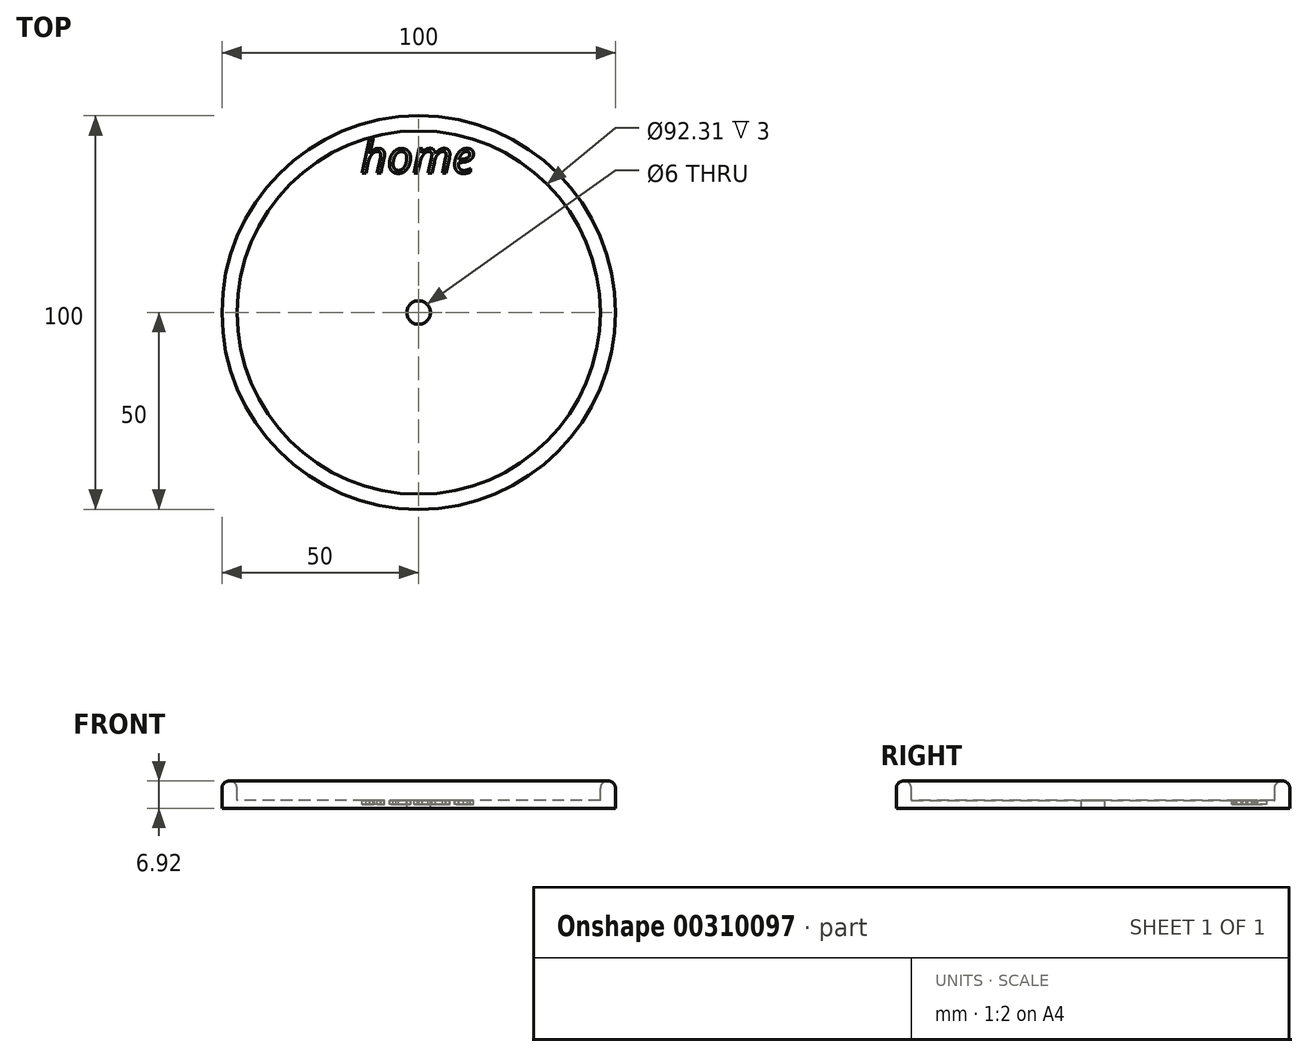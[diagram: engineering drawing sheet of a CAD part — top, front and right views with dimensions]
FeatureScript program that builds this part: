
annotation { "Feature Type Name" : "Feature", "Feature Type Description" : "" }
export const myFeature = defineFeature(function(context is Context, id is Id, definition is map)
    precondition{}
    {
        {
            var Q0;
            Q0=qCreatedBy(makeId("Front.planeOp"),FACE);
            var sketch = newSketch(context, id + "F0", { "sketchPlane" : qUnion([Q0])});
            skLineSegment(sketch, "E0", {"start": v(0, 11.93) * mm, "end": v(0, -12.11) * mm, "construction": true});
            skLineSegment(sketch, "E1", {"start": v(0, 0) * mm, "end": v(50, 0) * mm});
            skLineSegment(sketch, "E2", {"start": v(50, 0) * mm, "end": v(50, 5) * mm});
            skArc(sketch, "E3", {"start": v(50, 5) * mm, "mid": v(48.08, 6.92) * mm, "end": v(46.15, 5) * mm});
            skLineSegment(sketch, "E4", {"start": v(46.15, 5) * mm, "end": v(46.15, 2) * mm});
            skLineSegment(sketch, "E5", {"start": v(46.15, 2) * mm, "end": v(0, 2) * mm});
            skLineSegment(sketch, "E6", {"start": v(0, 2) * mm, "end": v(0, 0) * mm});
            skSolve(sketch);
        }
        {
            var Q0;
            Q0 = qSketchRegion(id + "F0", true);
            var Q1;
            Q1=sQuery(id+"F0.wireOp",EDGE,"E0");
            revolve(context, id + "F1", {"entities" : qUnion([Q0]), "axis" : qUnion([Q1]), "revolveType" : RevolveType.FULL});
        }
        {
            var Q0;
            Q0=makeQuery(id+"F1.opRevolve","SWEPT_FACE",FACE,{"disambiguationData":[OSD([sQuery(id+"F0.wireOp",EDGE,"E5")])]});
            var sketch = newSketch(context, id + "F2", { "sketchPlane" : qUnion([Q0])});
            skCircle(sketch, "E7", {"center": v(0, 0) * mm, "radius": 3 * mm});
            skSolve(sketch);
        }
        {
            var Q0;
            Q0 = qSketchRegion(id + "F2", true);
            extrude(context, id + "F3", {"entities" : qUnion([Q0]), "operationType" : NewBodyOperationType.REMOVE, "oppositeDirection" : true, "depth" : 25 * mm});
        }
        {
            var Q0;
            Q0=makeQuery(id+"F1.opRevolve","SWEPT_FACE",FACE,{"disambiguationData":[OSD([sQuery(id+"F0.wireOp",EDGE,"E5")])]});
            var sketch = newSketch(context, id + "F4", { "sketchPlane" : qUnion([Q0])});
            skText(sketch, "E8", { "text": "home", "fontName": "OpenSans-Italic.ttf"});
            const initialGuessF4  = {"E8": [-0.01468, 0.03542, 1, 0, 0.00833]};
            skSetInitialGuess(sketch, initialGuessF4);
            skSolve(sketch);
        }
        {
            var Q0;
            Q0 = qSketchRegion(id + "F4", true);
            extrude(context, id + "F5", {"entities" : qUnion([Q0]), "operationType" : NewBodyOperationType.REMOVE, "oppositeDirection" : true, "depth" : 1 * mm});
        }
    });
